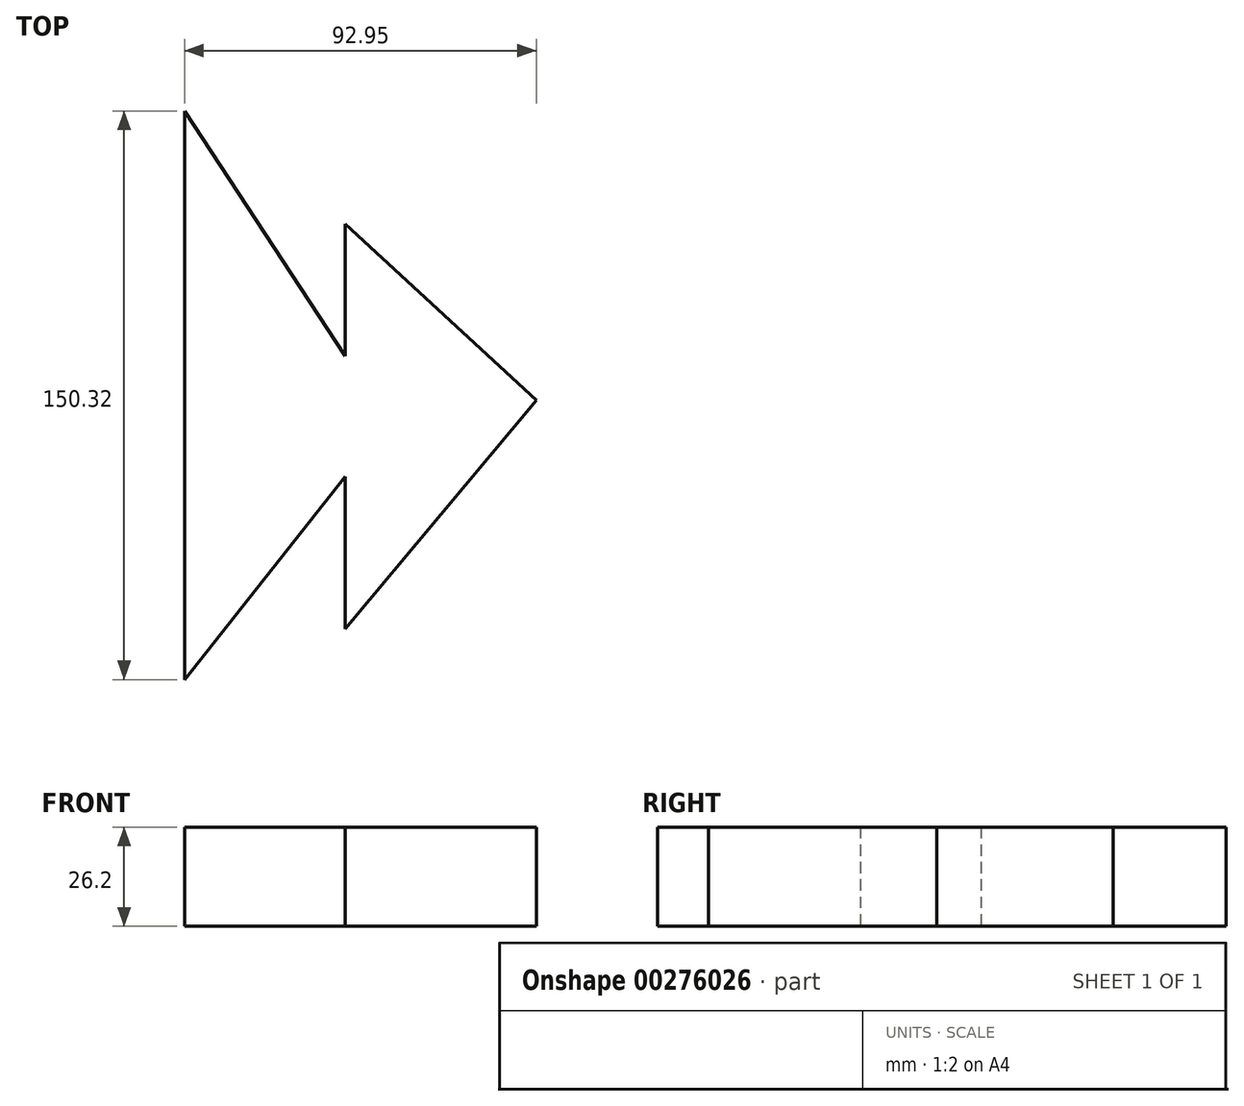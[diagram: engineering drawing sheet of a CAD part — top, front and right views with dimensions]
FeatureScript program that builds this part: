
annotation { "Feature Type Name" : "Feature", "Feature Type Description" : "" }
export const myFeature = defineFeature(function(context is Context, id is Id, definition is map)
    precondition{}
    {
        {
            var Q0;
            Q0=qCreatedBy(makeId("Top.planeOp"),FACE);
            var sketch = newSketch(context, id + "F0", { "sketchPlane" : qUnion([Q0])});
            skLineSegment(sketch, "E0", {"start": v(-42.46, 76.45) * mm, "end": v(-42.46, -73.87) * mm});
            skLineSegment(sketch, "E1", {"start": v(-42.46, -73.87) * mm, "end": v(0, -20.23) * mm});
            skLineSegment(sketch, "E2", {"start": v(0, -60.39) * mm, "end": v(0, -20.23) * mm});
            skLineSegment(sketch, "E3", {"start": v(0, -60.39) * mm, "end": v(50.5, 0) * mm});
            skLineSegment(sketch, "E4", {"start": v(50.5, 0) * mm, "end": v(0, 46.62) * mm});
            skLineSegment(sketch, "E5", {"start": v(0, 46.62) * mm, "end": v(0, 10.76) * mm});
            skLineSegment(sketch, "E6", {"start": v(0.57, 10.76) * mm, "end": v(-42.46, 76.45) * mm});
            skSolve(sketch);
        }
        {
            var Q0;
            {var subQ0=sQuery(id+"F0.wireOp",EDGE,"E0");Q0=makeQuery(id+"F0.imprint","IMPRINT",FACE,{"disambiguationData":[TD([[makeQuery(id+"F0.imprint","IMPRINT",EDGE,{"derivedFrom":subQ0}),1.0]])]});}
            extrude(context, id + "F1", {"entities" : qUnion([Q0]), "depth" : 26.2 * mm});
        }
    });
